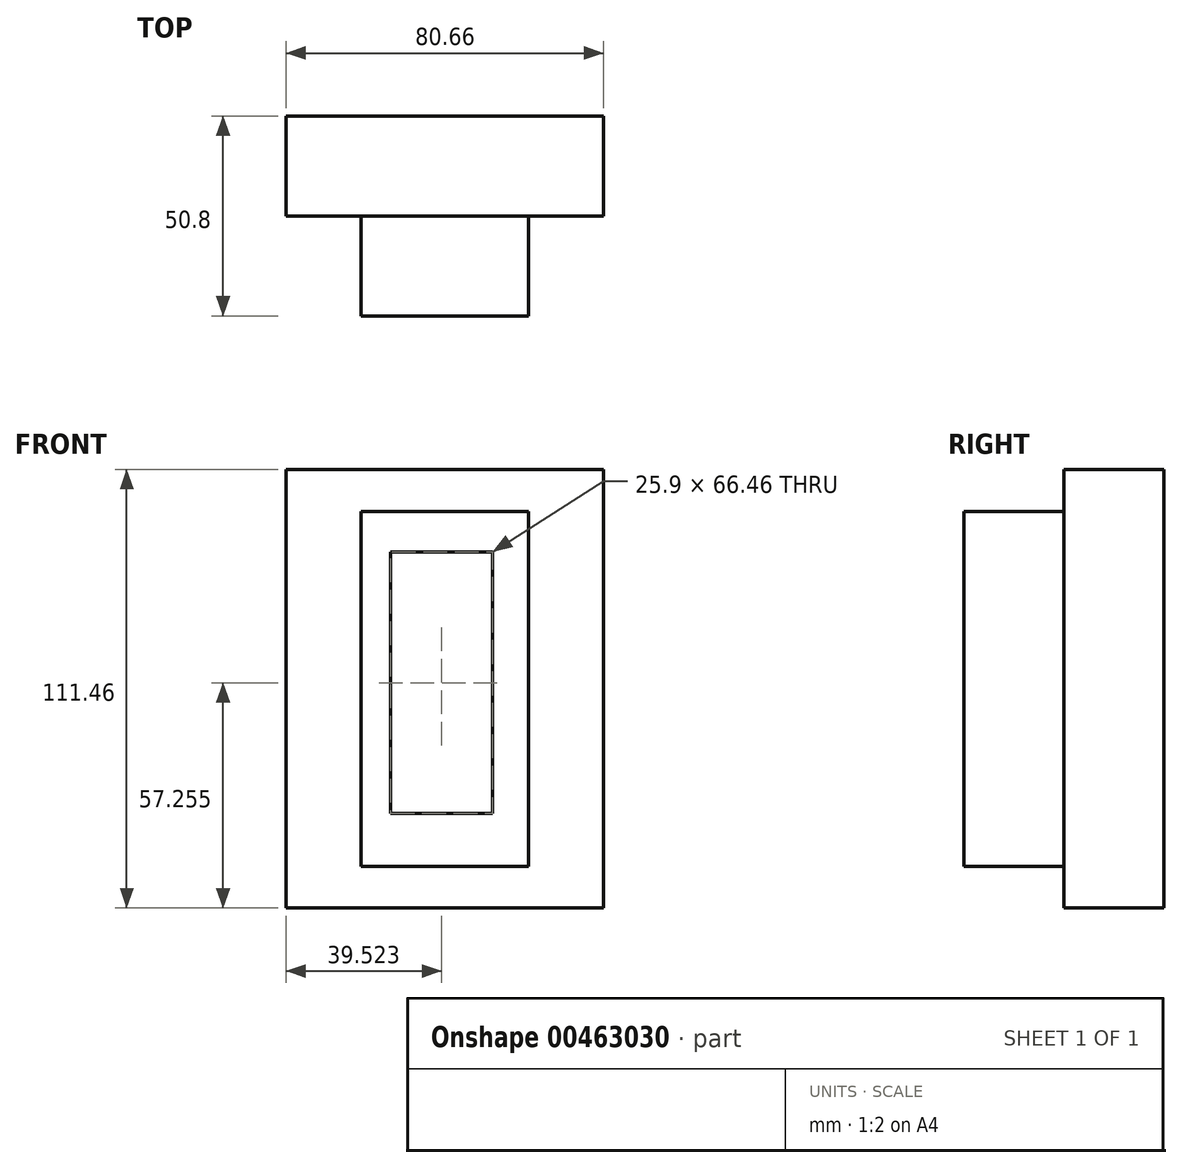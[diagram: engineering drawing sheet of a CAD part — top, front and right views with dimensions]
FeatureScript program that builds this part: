
annotation { "Feature Type Name" : "Feature", "Feature Type Description" : "" }
export const myFeature = defineFeature(function(context is Context, id is Id, definition is map)
    precondition{}
    {
        {
            var Q0;
            Q0=qCreatedBy(makeId("Front.planeOp"),FACE);
            var sketch = newSketch(context, id + "F0", { "sketchPlane" : qUnion([Q0])});
            skLineSegment(sketch, "E0.bottom", {"start": v(-40.33, -55.73) * mm, "end": v(40.33, -55.73) * mm});
            skLineSegment(sketch, "E0.top", {"start": v(-40.33, 55.73) * mm, "end": v(40.33, 55.73) * mm});
            skLineSegment(sketch, "E0.left", {"start": v(-40.33, -55.73) * mm, "end": v(-40.33, 55.73) * mm});
            skLineSegment(sketch, "E0.right", {"start": v(40.33, -55.73) * mm, "end": v(40.33, 55.73) * mm});
            skPoint(sketch, "E0.middle", {"position": v(0, 0) * mm});
            skSolve(sketch);
        }
        {
            var Q0;
            Q0=makeQuery(id+"F0.imprint","IMPRINT",FACE,{"disambiguationData":[TD([[makeQuery(id+"F0.imprint","IMPRINT",EDGE,{"derivedFrom":sQuery(id+"F0.wireOp",EDGE,"E0.bottom")}),1.0]])]});
            extrude(context, id + "F1", {"entities" : qUnion([Q0]), "depth" : 25.4 * mm});
        }
        {
            var Q0;
            Q0=qCreatedBy(makeId("Front.planeOp"),FACE);
            var sketch = newSketch(context, id + "F2", { "sketchPlane" : qUnion([Q0])});
            skLineSegment(sketch, "E1.bottom", {"start": v(-23.83, 44) * mm, "end": v(23.83, 44) * mm});
            skLineSegment(sketch, "E1.top", {"start": v(-23.83, -44) * mm, "end": v(23.83, -44) * mm});
            skLineSegment(sketch, "E1.left", {"start": v(-23.83, 44) * mm, "end": v(-23.83, -44) * mm});
            skLineSegment(sketch, "E1.right", {"start": v(23.83, 44) * mm, "end": v(23.83, -44) * mm});
            skPoint(sketch, "E1.middle", {"position": v(0, 0) * mm});
            skSolve(sketch);
        }
        {
            var Q0;
            Q0=makeQuery(id+"F2.imprint","IMPRINT",FACE,{"disambiguationData":[TD([[makeQuery(id+"F2.imprint","IMPRINT",EDGE,{"derivedFrom":sQuery(id+"F2.wireOp",EDGE,"E1.bottom")}),-1.0]])]});
            extrude(context, id + "F3", {"entities" : qUnion([Q0]), "operationType" : NewBodyOperationType.ADD, "depth" : 25.4 * mm});
        }
        {
            var Q0;
            Q0=makeQuery(id+"F1.opExtrude","CAP_FACE",FACE,{"disambiguationData":[OSD([sQuery(id+"F0.wireOp",EDGE,"E0.bottom"),sQuery(id+"F0.wireOp",EDGE,"E0.top"),sQuery(id+"F0.wireOp",EDGE,"E0.left"),sQuery(id+"F0.wireOp",EDGE,"E0.right")])],"isStart":false});
            var sketch = newSketch(context, id + "F4", { "sketchPlane" : qUnion([Q0])});
            skLineSegment(sketch, "E2.bottom", {"start": v(-21.3, -45.09) * mm, "end": v(21.3, -45.09) * mm});
            skLineSegment(sketch, "E2.top", {"start": v(-21.3, 45.09) * mm, "end": v(21.3, 45.09) * mm});
            skLineSegment(sketch, "E2.left", {"start": v(-21.3, -45.09) * mm, "end": v(-21.3, 45.09) * mm});
            skLineSegment(sketch, "E2.right", {"start": v(21.3, -45.09) * mm, "end": v(21.3, 45.09) * mm});
            skPoint(sketch, "E2.middle", {"position": v(0, 0) * mm});
            skLineSegment(sketch, "E3.bottom", {"start": v(-13.76, -31.7) * mm, "end": v(12.14, -31.7) * mm});
            skLineSegment(sketch, "E3.top", {"start": v(-13.76, 34.76) * mm, "end": v(12.14, 34.76) * mm});
            skLineSegment(sketch, "E3.left", {"start": v(-13.76, -31.7) * mm, "end": v(-13.76, 34.76) * mm});
            skLineSegment(sketch, "E3.right", {"start": v(12.14, -31.7) * mm, "end": v(12.14, 34.76) * mm});
            skPoint(sketch, "E3.middle", {"position": v(-0.8, 1.52) * mm});
            skSolve(sketch);
        }
        {
            var Q0;
            Q0=makeQuery(id+"F4.imprint","IMPRINT",FACE,{"disambiguationData":[TD([[makeQuery(id+"F4.imprint","IMPRINT",EDGE,{"derivedFrom":sQuery(id+"F4.wireOp",EDGE,"E2.bottom")}),1.0]])]});
            extrude(context, id + "F5", {"entities" : qUnion([Q0]), "operationType" : NewBodyOperationType.ADD, "depth" : 25.4 * mm});
        }
        {
            var Q0;
            Q0=makeQuery(id+"F5.boolean.opBoolean","SPLIT",FACE,{"disambiguationData":[TD([makeQuery(id+"F5.opExtrude","SWEPT_FACE",FACE,{"disambiguationData":[OSD([sQuery(id+"F4.wireOp",EDGE,"E3.bottom")])]})])],"derivedFrom":makeQuery(id+"F1.opExtrude","CAP_FACE",FACE,{"disambiguationData":[OSD([sQuery(id+"F0.wireOp",EDGE,"E0.bottom"),sQuery(id+"F0.wireOp",EDGE,"E0.top"),sQuery(id+"F0.wireOp",EDGE,"E0.left"),sQuery(id+"F0.wireOp",EDGE,"E0.right")])],"isStart":false})});
            var sketch = newSketch(context, id + "F6", { "sketchPlane" : qUnion([Q0])});
            skLineSegment(sketch, "E4.bottom", {"start": v(-13.76, 34.76) * mm, "end": v(12.14, 34.76) * mm});
            skLineSegment(sketch, "E4.top", {"start": v(-13.76, -31.7) * mm, "end": v(12.14, -31.7) * mm});
            skLineSegment(sketch, "E4.left", {"start": v(-13.76, 34.76) * mm, "end": v(-13.76, -31.7) * mm});
            skLineSegment(sketch, "E4.right", {"start": v(12.14, 34.76) * mm, "end": v(12.14, -31.7) * mm});
            skSolve(sketch);
        }
        {
            var Q0;
            Q0=makeQuery(id+"F6.imprint","IMPRINT",FACE,{"disambiguationData":[TD([[makeQuery(id+"F6.imprint","IMPRINT",EDGE,{"derivedFrom":sQuery(id+"F6.wireOp",EDGE,"E4.bottom")}),-1.0]])]});
            extrude(context, id + "F7", {"entities" : qUnion([Q0]), "operationType" : NewBodyOperationType.REMOVE, "oppositeDirection" : true, "depth" : 31.6 * mm});
        }
    });
